# Revit family: OASIS SH3P-6032 ABF
name_source: partatom
category: Plumbing Fixtures
units: mm (PartAtom-declared; Revit-internal decimal feet)

## family parameters
Always vertical = Yes
Cut with Voids When Loaded = No
OmniClass Number = 23.45.05.14.17.11
OmniClass Title = Shower Compartments
Part Type = Normal
Room Calculation Point = No
Round Connector Dimension = Use Diameter
Shared = No
Work Plane-Based = No

## types (5) — shared parameters
BIM Model By = www.shive-hattery.com
Cold Water Connector = Cold Water Connection
Color = <By Category>
Default Elevation = 0"
Grab Bar Finish = <By Category>
Hot Water Connector = Hot Water Connection
Manufacturer = OASIS
Sanitary Connector = Sanitary Connection
Seat Finish = <By Category>
Stainless steel = <By Category>
Type Comments = SHOWER
URL = www.oasisbath.com
Waste Connection = No

## per-type parameters (varying)
| type | Bar_Horz_Back | Bar_Horz_Right | Bar_Vert | Model | N0_Bar_Vert | Seat_Fold | Shower Rod |
| Base model, 3SF, 3SM, & FH packages | No | No | No | SH3P-6032 ABF/(3SF,3SM,FH) | Yes | No | No |
| BP1-60 package | Yes | Yes | No | SH3P-6032 ABF/BP1-60 | Yes | No | No |
| BP2-60 package | Yes | Yes | Yes | SH3P-6032 ABF/BP2-60 | No | No | No |
| TLV package | Yes | Yes | Yes | SH3P-6032 ABF/TLV | No | Yes | Yes |
| TL package | Yes | Yes | No | SH3P-6032 ABF/TL | Yes | Yes | Yes |

## geometry (parser evidence)
native form markers: Blend x2, Sweep x14
no freeform markers — native parametric forms only
